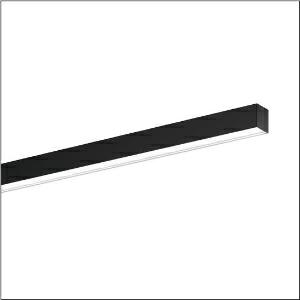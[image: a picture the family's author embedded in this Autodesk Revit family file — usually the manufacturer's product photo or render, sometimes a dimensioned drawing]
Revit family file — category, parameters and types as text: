
# Revit family: silica_r__21_51mx20dc45bb_0fdd
name_source: partatom
category: Lighting Fixtures
units: mm (PartAtom-declared; Revit-internal decimal feet)

## family parameters
Cut with Voids When Loaded = No
Host = Face
Light Source = No
Part Type = Normal
Room Calculation Point = No
Round Connector Dimension = Use Diameter
Shared = No

## types (1)
- --- (1 x LED, 6000 lm, 40.1 W, 4000K)
    Apparent Load = 40 VA
    CIE Flux Codes = 48 79 96 100 100
    Color Rendering = 80
    Color Temperature = 4000K
    Default Elevation = 1800 mm
    Description = Silica® 21, office luminaire, primary optical cover: cover, of PMMA, opal, light emission: direct distribution, primary light characteristic: symmetric, installation type: surface-mounted, LED, rated luminous flux: 6.000lm, luminous efficacy: 150lm/W, light colour: 840, colour temperature: 4000K, with terminal, 3+2-pole, max. 2.5mm², mains connection: 220..240V, AC, 50/60Hz, rated input power: 40.1W, luminaire housing, of aluminium, jet black (RAL 9005), length: 3.004mm, width: 53mm, height: 53mm, protection rating (complete): IP20, insulation class (complete): insulation class I (protective earthing), certification: CE, permissible operating ambient temperature: 0..+35°C, standard: EN 50419, packaging unit: 1 piece
    Height = 0 mm  [stored 0 ft]
    Lamp = 1 x LED
    Lamp Light Flux = 6000 lm
    Lamp Power = 40.1 W
    Lamp count = 1
    Length = 3004 mm
    Luminous efficacy = 150 lm/W
    Manufacturer = Siteco
    ModVariant = No
    Model = 51MX20DC45BB
    Mounting Place = Ceiling
    Mounting Type = Recessed
    Number of Poles = 1
    OnlyDefault = Yes
    Power Factor = 1
    Product Name = Silica® 21
    Product group = office luminaire | ceiling recessed
    ProductGroupID = 400
    Protection Class = Protection class I
    Protection Degree = IP 20
    RLX_Detail_Level = 1
    RLX_Emergency_Light_Flux = 0 lm
    RLX_Emergency_Type = 0
    RLX_Emergency_Type_DB = No
    RlxData = <blob elided: 28865 chars, md5=506966f0>
    Socket = socket
    Standby Power = 0 W
    System Light Flux = 6000 lm
    System Power = 40 W
    Type Comments = factory setting: luminous flux: 100 % | dim-lin: 254 | 218 mA
    Type Image = l_1335925.jpg
    URL = http://relux.com
    VarID = @adj_086771
    Voltage = 0 V
    Weight = 0.00 kg
    Width = 53 mm

note: [stored X ft] marks values corroborated as IEEE doubles in the binary element streams (Revit-internal decimal feet)

## geometry (parser evidence)
native form markers: Blend x4, Sweep x10
no freeform markers — native parametric forms only
